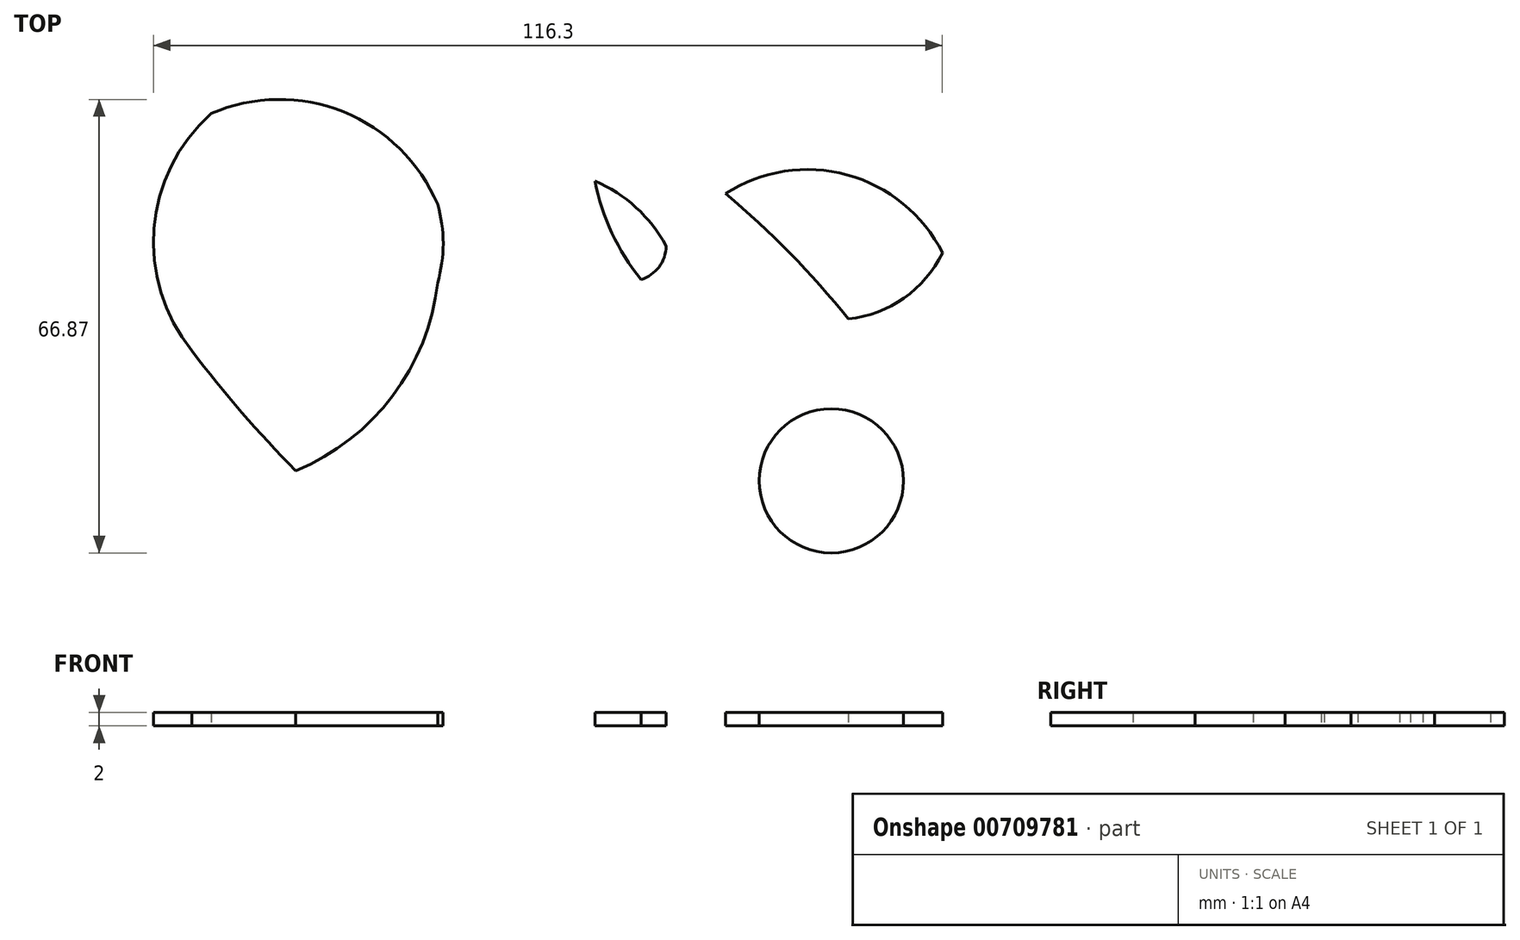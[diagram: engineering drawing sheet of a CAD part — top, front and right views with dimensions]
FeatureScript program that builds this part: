
annotation { "Feature Type Name" : "Feature", "Feature Type Description" : "" }
export const myFeature = defineFeature(function(context is Context, id is Id, definition is map)
    precondition{}
    {
        {
            var Q0;
            Q0=qCreatedBy(makeId("Top.planeOp"),FACE);
            var sketch = newSketch(context, id + "F0", { "sketchPlane" : qUnion([Q0])});
            skArc(sketch, "E0", {"start": v(103.96, 46.7) * mm, "mid": v(89.93, 58.2) * mm, "end": v(72, 55.43) * mm});
            skArc(sketch, "E1", {"start": v(90.11, 36.97) * mm, "mid": v(98.3, 40.04) * mm, "end": v(103.96, 46.7) * mm});
            skArc(sketch, "E2", {"start": v(90.11, 36.97) * mm, "mid": v(81.5, 46.64) * mm, "end": v(72, 55.43) * mm});
            skArc(sketch, "E3", {"start": v(52.77, 57.29) * mm, "mid": v(55.25, 49.61) * mm, "end": v(59.52, 42.77) * mm});
            skArc(sketch, "E4", {"start": v(59.52, 42.77) * mm, "mid": v(62.2, 44.63) * mm, "end": v(63.21, 47.72) * mm});
            skArc(sketch, "E5", {"start": v(63.21, 47.72) * mm, "mid": v(58.8, 53.4) * mm, "end": v(52.77, 57.29) * mm});
            skArc(sketch, "E6", {"start": v(-3.82, 67.28) * mm, "mid": v(-12.25, 50.34) * mm, "end": v(-6.67, 32.26) * mm});
            skArc(sketch, "E7", {"start": v(-6.67, 32.26) * mm, "mid": v(0.68, 23.17) * mm, "end": v(8.64, 14.6) * mm});
            skArc(sketch, "E8", {"start": v(8.64, 14.6) * mm, "mid": v(22.9, 25.6) * mm, "end": v(29.55, 42.32) * mm});
            skArc(sketch, "E9", {"start": v(29.55, 42.32) * mm, "mid": v(30.37, 48.08) * mm, "end": v(29.55, 53.84) * mm});
            skArc(sketch, "E10", {"start": v(29.55, 53.84) * mm, "mid": v(15.66, 67.5) * mm, "end": v(-3.82, 67.28) * mm});
            skCircle(sketch, "E11", {"center": v(87.58, 13.1) * mm, "radius": 10.63 * mm});
            skSolve(sketch);
        }
        {
            var Q0;
            Q0=makeQuery(id+"F0.imprint","IMPRINT",FACE,{"disambiguationData":[TD([[makeQuery(id+"F0.imprint","IMPRINT",EDGE,{"derivedFrom":sQuery(id+"F0.wireOp",EDGE,"E6")}),1.0]])]});
            var Q1;
            Q1=makeQuery(id+"F0.imprint","IMPRINT",FACE,{"disambiguationData":[TD([[makeQuery(id+"F0.imprint","IMPRINT",EDGE,{"derivedFrom":sQuery(id+"F0.wireOp",EDGE,"E0")}),1.0]])]});
            var Q2;
            Q2=makeQuery(id+"F0.imprint","IMPRINT",FACE,{"disambiguationData":[TD([[makeQuery(id+"F0.imprint","IMPRINT",EDGE,{"derivedFrom":sQuery(id+"F0.wireOp",EDGE,"E11")}),1.0]])]});
            var Q3;
            Q3=makeQuery(id+"F0.imprint","IMPRINT",FACE,{"disambiguationData":[TD([[makeQuery(id+"F0.imprint","IMPRINT",EDGE,{"derivedFrom":sQuery(id+"F0.wireOp",EDGE,"E3")}),1.0]])]});
            extrude(context, id + "F1", {"entities" : qUnion([Q0, Q1, Q2, Q3]), "depth" : 2 * mm, "offsetDistance" : 25.4 * mm});
        }
    });
